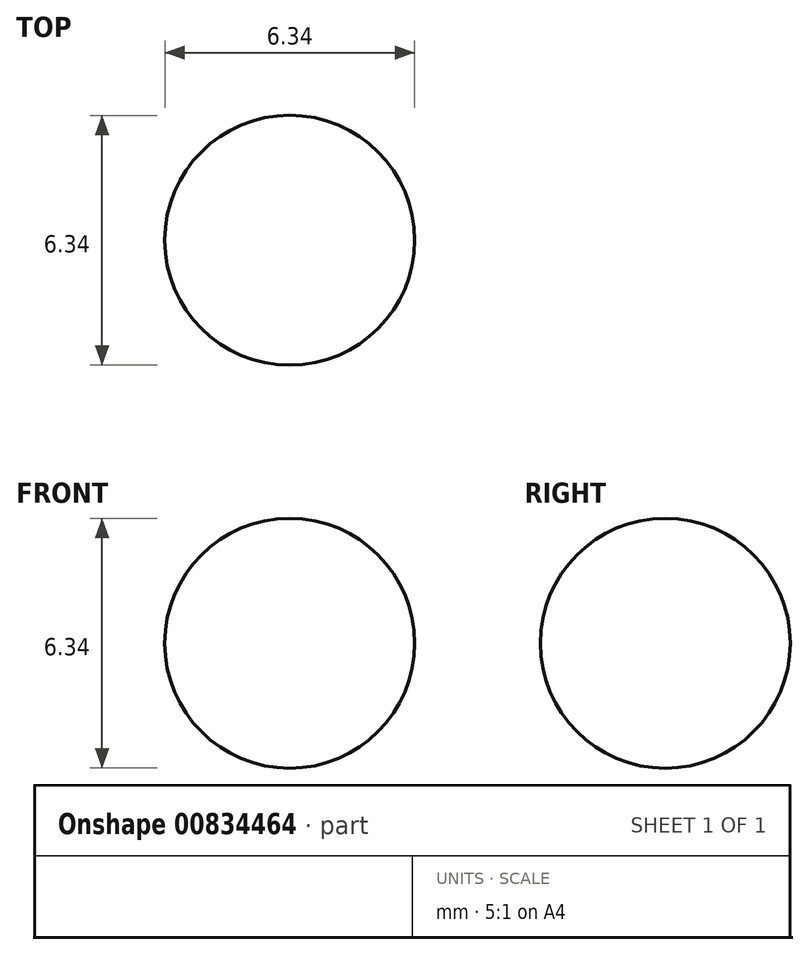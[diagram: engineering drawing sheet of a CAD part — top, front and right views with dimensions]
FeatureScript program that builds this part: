
annotation { "Feature Type Name" : "Feature", "Feature Type Description" : "" }
export const myFeature = defineFeature(function(context is Context, id is Id, definition is map)
    precondition{}
    {
        {
            var Q0;
            Q0=qCreatedBy(makeId("Front.planeOp"),FACE);
            var sketch = newSketch(context, id + "F0", { "sketchPlane" : qUnion([Q0])});
            skCircle(sketch, "E0", {"center": v(0, 0) * mm, "radius": 3.18 * mm});
            skLineSegment(sketch, "E1", {"start": v(0, 3.18) * mm, "end": v(0, -3.18) * mm});
            skSolve(sketch);
        }
        {
            var Q0;
            {var subQ0=sQuery(id+"F0.wireOp",EDGE,"E1");Q0=makeQuery(id+"F0.imprint","IMPRINT",FACE,{"disambiguationData":[TD([[makeQuery(id+"F0.imprint","IMPRINT",EDGE,{"derivedFrom":subQ0}),1.0]])]});}
            var Q1;
            Q1=sQuery(id+"F0.wireOp",EDGE,"E1");
            revolve(context, id + "F1", {"surfaceOperationType" : NewSurfaceOperationType.NEW, "entities" : qUnion([Q0]), "axis" : qUnion([Q1]), "revolveType" : RevolveType.FULL});
        }
    });
